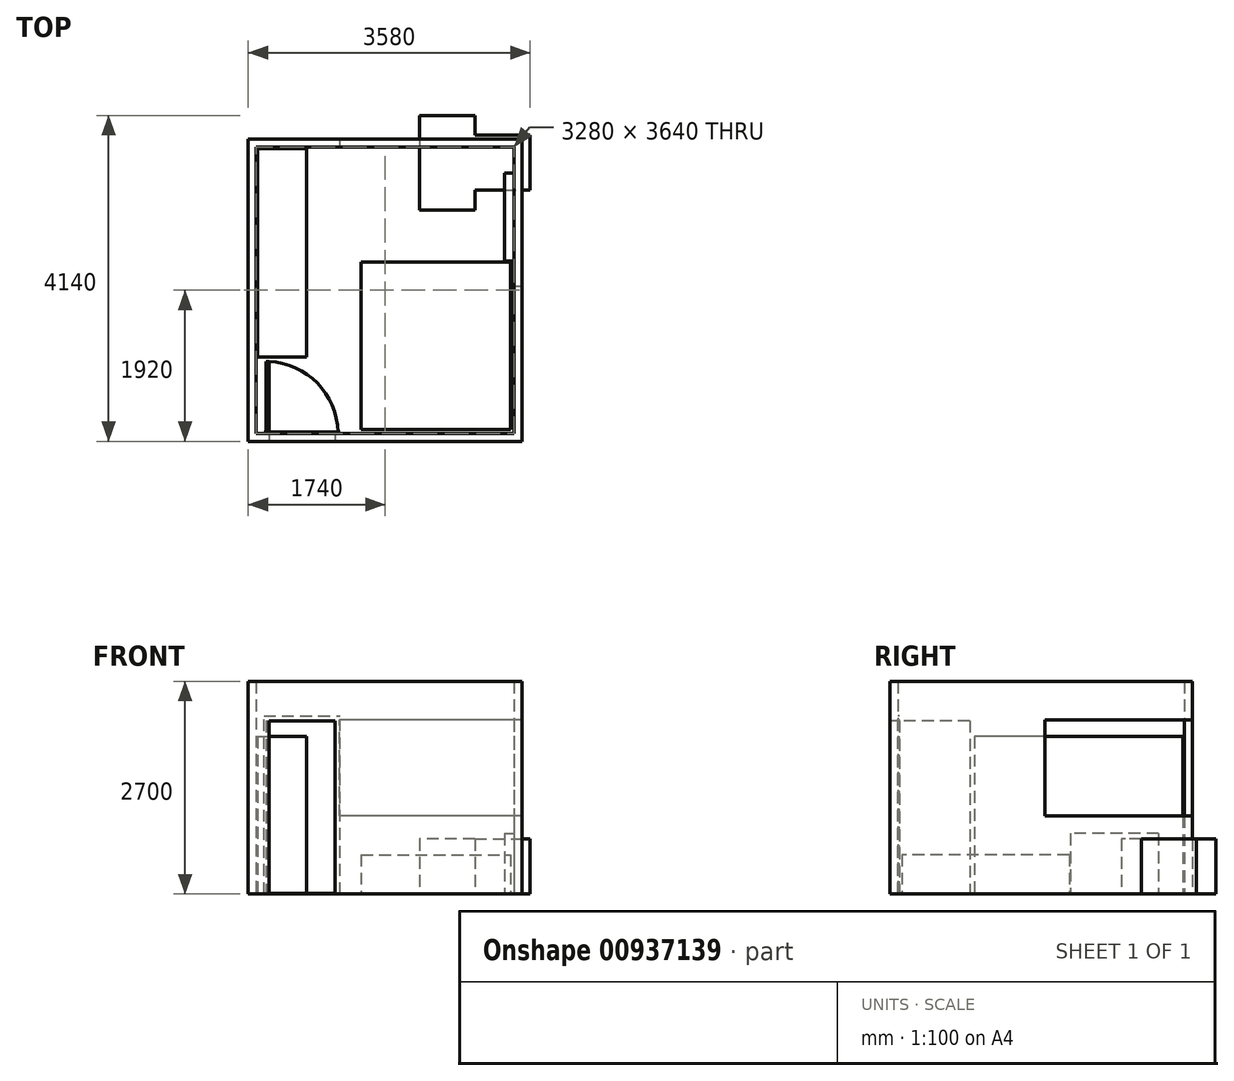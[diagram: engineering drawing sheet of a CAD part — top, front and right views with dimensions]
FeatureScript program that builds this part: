
annotation { "Feature Type Name" : "Feature", "Feature Type Description" : "" }
export const myFeature = defineFeature(function(context is Context, id is Id, definition is map)
    precondition{}
    {
        {
            var Q0;
            Q0=qCreatedBy(makeId("Top.planeOp"),FACE);
            var sketch = newSketch(context, id + "F0", { "sketchPlane" : qUnion([Q0])});
            skLineSegment(sketch, "E0.bottom", {"start": v(-3280, 3640) * mm, "end": v(0, 3640) * mm});
            skLineSegment(sketch, "E0.top", {"start": v(-3280, 0) * mm, "end": v(0, 0) * mm});
            skLineSegment(sketch, "E0.left", {"start": v(-3280, 3640) * mm, "end": v(-3280, 0) * mm});
            skLineSegment(sketch, "E0.right", {"start": v(0, 3640) * mm, "end": v(0, 0) * mm});
            skLineSegment(sketch, "E1.0", {"start": v(-3380, 3740) * mm, "end": v(100, 3740) * mm});
            skLineSegment(sketch, "E1.1", {"start": v(-3380, 3740) * mm, "end": v(-3380, -100) * mm});
            skLineSegment(sketch, "E1.2", {"start": v(-3380, -100) * mm, "end": v(100, -100) * mm});
            skLineSegment(sketch, "E1.3", {"start": v(100, 3740) * mm, "end": v(100, -100) * mm});
            skSolve(sketch);
        }
        {
            var Q0;
            Q0=makeQuery(id+"F0.imprint","IMPRINT",FACE,{"disambiguationData":[TD([[makeQuery(id+"F0.imprint","IMPRINT",EDGE,{"derivedFrom":sQuery(id+"F0.wireOp",EDGE,"E0.bottom")}),1.0]])]});
            extrude(context, id + "F1", {"entities" : qUnion([Q0]), "depth" : 2700 * mm, "offsetDistance" : 25 * mm});
        }
        {
            var Q0;
            Q0=makeQuery(id+"F1.opExtrude","SWEPT_FACE",FACE,{"disambiguationData":[OSD([sQuery(id+"F0.wireOp",EDGE,"E0.top")])]});
            var sketch = newSketch(context, id + "F2", { "sketchPlane" : qUnion([Q0])});
            skLineSegment(sketch, "E2.bottom", {"start": v(3115, 0) * mm, "end": v(2275, 0) * mm});
            skLineSegment(sketch, "E2.top", {"start": v(3115, 2200) * mm, "end": v(2275, 2200) * mm});
            skLineSegment(sketch, "E2.left", {"start": v(3115, 0) * mm, "end": v(3115, 2200) * mm});
            skLineSegment(sketch, "E2.right", {"start": v(2275, 0) * mm, "end": v(2275, 2200) * mm});
            skLineSegment(sketch, "E3.bottom", {"start": v(3180, 0) * mm, "end": v(2210, 0) * mm});
            skLineSegment(sketch, "E3.top", {"start": v(3180, 2265) * mm, "end": v(2210, 2265) * mm});
            skLineSegment(sketch, "E3.left", {"start": v(3180, 0) * mm, "end": v(3180, 2265) * mm});
            skLineSegment(sketch, "E3.right", {"start": v(2210, 0) * mm, "end": v(2210, 2265) * mm});
            skSolve(sketch);
        }
        {
            var Q0;
            Q0=makeQuery(id+"F2.imprint","IMPRINT",FACE,{"disambiguationData":[TD([[makeQuery(id+"F2.imprint","IMPRINT",EDGE,{"derivedFrom":sQuery(id+"F2.wireOp",EDGE,"E2.top")}),-1.0]])]});
            extrude(context, id + "F3", {"entities" : qUnion([Q0]), "operationType" : NewBodyOperationType.ADD, "depth" : 20 * mm, "offsetDistance" : 25 * mm});
        }
        {
            var Q0;
            {var subQ1=sQuery(id+"F0.wireOp",EDGE,"E0.top");Q0=makeQuery(id+"F3.boolean.opBoolean","SPLIT",FACE,{"disambiguationData":[TD([makeQuery(id+"F3.opExtrude","SWEPT_FACE",FACE,{"disambiguationData":[OSD([sQuery(id+"F2.wireOp",EDGE,"E2.top")])]})])],"derivedFrom":makeQuery(id+"F1.opExtrude","SWEPT_FACE",FACE,{"disambiguationData":[OSD([subQ1])]})});}
            extrude(context, id + "F4", {"entities" : qUnion([Q0]), "operationType" : NewBodyOperationType.REMOVE, "endBound" : BoundingType.UP_TO_NEXT, "oppositeDirection" : true, "depth" : 25 * mm, "offsetDistance" : 25 * mm});
        }
        {
            var Q0;
            Q0=makeQuery(id+"F1.opExtrude","SWEPT_FACE",FACE,{"disambiguationData":[OSD([sQuery(id+"F0.wireOp",EDGE,"E0.right")])]});
            var sketch = newSketch(context, id + "F5", { "sketchPlane" : qUnion([Q0])});
            skLineSegment(sketch, "E4.bottom", {"start": v(-3640, 2210) * mm, "end": v(-1870, 2210) * mm});
            skLineSegment(sketch, "E4.top", {"start": v(-3640, 990) * mm, "end": v(-1870, 990) * mm});
            skLineSegment(sketch, "E4.left", {"start": v(-3640, 2210) * mm, "end": v(-3640, 990) * mm});
            skLineSegment(sketch, "E4.right", {"start": v(-1870, 2210) * mm, "end": v(-1870, 990) * mm});
            skSolve(sketch);
        }
        {
            var Q0;
            Q0 = qSketchRegion(id + "F5", true);
            extrude(context, id + "F6", {"entities" : qUnion([Q0]), "operationType" : NewBodyOperationType.REMOVE, "endBound" : BoundingType.UP_TO_NEXT, "oppositeDirection" : true, "depth" : 25 * mm, "offsetDistance" : 25 * mm});
        }
        {
            var Q0;
            Q0=makeQuery(id+"F6.boolean.opBoolean","MERGE",FACE,{"derivedFrom":[makeQuery(id+"F1.opExtrude","SWEPT_FACE",FACE,{"disambiguationData":[OSD([sQuery(id+"F0.wireOp",EDGE,"E0.bottom")])]})],"fromTools":[makeQuery(id+"F6.opExtrude","SWEPT_FACE",FACE,{"disambiguationData":[OSD([sQuery(id+"F5.wireOp",EDGE,"E4.left")])]})]});
            var sketch = newSketch(context, id + "F7", { "sketchPlane" : qUnion([Q0])});
            skLineSegment(sketch, "E5.bottom", {"start": v(100, 990) * mm, "end": v(-2220, 990) * mm});
            skLineSegment(sketch, "E5.top", {"start": v(100, 2210) * mm, "end": v(-2220, 2210) * mm});
            skLineSegment(sketch, "E5.left", {"start": v(100, 990) * mm, "end": v(100, 2210) * mm});
            skLineSegment(sketch, "E5.right", {"start": v(-2220, 990) * mm, "end": v(-2220, 2210) * mm});
            skSolve(sketch);
        }
        {
            var Q0;
            Q0 = qSketchRegion(id + "F7", true);
            extrude(context, id + "F8", {"entities" : qUnion([Q0]), "operationType" : NewBodyOperationType.REMOVE, "endBound" : BoundingType.UP_TO_NEXT, "oppositeDirection" : true, "depth" : 25 * mm, "offsetDistance" : 25 * mm});
        }
        {
            var Q0;
            Q0=makeQuery(id+"F1.opExtrude","SWEPT_FACE",FACE,{"disambiguationData":[OSD([sQuery(id+"F0.wireOp",EDGE,"E0.right")])]});
            var sketch = newSketch(context, id + "F9", { "sketchPlane" : qUnion([Q0])});
            skLineSegment(sketch, "E6.bottom", {"start": v(-3310, 770) * mm, "end": v(-2190, 770) * mm});
            skLineSegment(sketch, "E6.top", {"start": v(-3310, 0) * mm, "end": v(-2190, 0) * mm});
            skLineSegment(sketch, "E6.left", {"start": v(-3310, 770) * mm, "end": v(-3310, 0) * mm});
            skLineSegment(sketch, "E6.right", {"start": v(-2190, 770) * mm, "end": v(-2190, 0) * mm});
            skSolve(sketch);
        }
        {
            var Q0;
            Q0 = qSketchRegion(id + "F9", true);
            extrude(context, id + "F10", {"entities" : qUnion([Q0]), "operationType" : NewBodyOperationType.ADD, "depth" : 125 * mm, "offsetDistance" : 25 * mm});
        }
        {
            var Q0;
            {var subQ0=sQuery(id+"F2.wireOp",EDGE,"E3.bottom");var subQ1=sQuery(id+"F0.wireOp",EDGE,"E0.top");Q0=makeQuery(id+"F3.boolean.opBoolean","MERGE",FACE,{"derivedFrom":[makeQuery(id+"F1.opExtrude","CAP_FACE",FACE,{"disambiguationData":[OSD([sQuery(id+"F0.wireOp",EDGE,"E0.bottom"),subQ1,sQuery(id+"F0.wireOp",EDGE,"E0.left"),sQuery(id+"F0.wireOp",EDGE,"E0.right"),sQuery(id+"F0.wireOp",EDGE,"E1.0"),sQuery(id+"F0.wireOp",EDGE,"E1.1"),sQuery(id+"F0.wireOp",EDGE,"E1.2"),sQuery(id+"F0.wireOp",EDGE,"E1.3")])],"isStart":true}),makeQuery(id+"F3.opExtrude","SWEPT_FACE",FACE,{"disambiguationData":[OSD([subQ0]),TDD([makeQuery(id+"F2.imprint","IMPRINT",EDGE,{"disambiguationData":[TD([[makeQuery(id+"F2.imprint","INTERSECT",VERTEX,{"derivedFrom":[sQuery(id+"F2.wireOp",EDGE,"E2.left"),subQ0]}),1.0]])],"derivedFrom":subQ0})])]}),makeQuery(id+"F3.opExtrude","SWEPT_FACE",FACE,{"disambiguationData":[OSD([subQ0]),TDD([makeQuery(id+"F2.imprint","IMPRINT",EDGE,{"disambiguationData":[TD([[makeQuery(id+"F2.imprint","INTERSECT",VERTEX,{"derivedFrom":[sQuery(id+"F2.wireOp",EDGE,"E2.right"),subQ0]}),-1.0]])],"derivedFrom":subQ0})])]})]});}
            var sketch = newSketch(context, id + "F11", { "sketchPlane" : qUnion([Q0])});
            skLineSegment(sketch, "E7.bottom", {"start": v(-3115, -20) * mm, "end": v(-3155, -20) * mm});
            skLineSegment(sketch, "E7.top", {"start": v(-3115, -915) * mm, "end": v(-3155, -915) * mm});
            skLineSegment(sketch, "E7.left", {"start": v(-3115, -915) * mm, "end": v(-3115, -20) * mm});
            skLineSegment(sketch, "E7.right", {"start": v(-3155, -915) * mm, "end": v(-3155, -20) * mm});
            skSolve(sketch);
        }
        {
            var Q0;
            Q0 = qSketchRegion(id + "F11", true);
            extrude(context, id + "F12", {"entities" : qUnion([Q0]), "operationType" : NewBodyOperationType.ADD, "oppositeDirection" : true, "depth" : 2200 * mm, "offsetDistance" : 25 * mm});
        }
        {
            var Q0;
            {var subQ0=sQuery(id+"F2.wireOp",EDGE,"E3.bottom");var subQ1=sQuery(id+"F0.wireOp",EDGE,"E0.top");Q0=makeQuery(id+"F10.boolean.opBoolean","MERGE",FACE,{"derivedFrom":[makeQuery(id+"F12.boolean.opBoolean","MERGE",FACE,{"derivedFrom":[makeQuery(id+"F3.boolean.opBoolean","MERGE",FACE,{"derivedFrom":[makeQuery(id+"F1.opExtrude","CAP_FACE",FACE,{"disambiguationData":[OSD([sQuery(id+"F0.wireOp",EDGE,"E0.bottom"),subQ1,sQuery(id+"F0.wireOp",EDGE,"E0.left"),sQuery(id+"F0.wireOp",EDGE,"E0.right"),sQuery(id+"F0.wireOp",EDGE,"E1.0"),sQuery(id+"F0.wireOp",EDGE,"E1.1"),sQuery(id+"F0.wireOp",EDGE,"E1.2"),sQuery(id+"F0.wireOp",EDGE,"E1.3")])],"isStart":true}),makeQuery(id+"F3.opExtrude","SWEPT_FACE",FACE,{"disambiguationData":[OSD([subQ0]),TDD([makeQuery(id+"F2.imprint","IMPRINT",EDGE,{"disambiguationData":[TD([[makeQuery(id+"F2.imprint","INTERSECT",VERTEX,{"derivedFrom":[sQuery(id+"F2.wireOp",EDGE,"E2.left"),subQ0]}),1.0]])],"derivedFrom":subQ0})])]}),makeQuery(id+"F3.opExtrude","SWEPT_FACE",FACE,{"disambiguationData":[OSD([subQ0]),TDD([makeQuery(id+"F2.imprint","IMPRINT",EDGE,{"disambiguationData":[TD([[makeQuery(id+"F2.imprint","INTERSECT",VERTEX,{"derivedFrom":[sQuery(id+"F2.wireOp",EDGE,"E2.right"),subQ0]}),-1.0]])],"derivedFrom":subQ0})])]})]}),makeQuery(id+"F12.opExtrude","CAP_FACE",FACE,{"disambiguationData":[OSD([sQuery(id+"F11.wireOp",EDGE,"E7.bottom"),sQuery(id+"F11.wireOp",EDGE,"E7.top"),sQuery(id+"F11.wireOp",EDGE,"E7.left"),sQuery(id+"F11.wireOp",EDGE,"E7.right")])],"isStart":true})]}),makeQuery(id+"F10.opExtrude","SWEPT_FACE",FACE,{"disambiguationData":[OSD([sQuery(id+"F9.wireOp",EDGE,"E6.top")])]})]});}
            var sketch = newSketch(context, id + "F13", { "sketchPlane" : qUnion([Q0])});
            skArc(sketch, "E8", {"start": v(-3115, -915) * mm, "mid": v(-2500.34, -640.5) * mm, "end": v(-2239.34, -20) * mm});
            skLineSegment(sketch, "E9", {"start": v(-2239.34, -20) * mm, "end": v(-3115, 0) * mm});
            skLineSegment(sketch, "E10", {"start": v(-3115, 0) * mm, "end": v(-3115, -915) * mm});
            skSolve(sketch);
        }
        {
            var Q0;
            Q0 = qSketchRegion(id + "F13", true);
            extrude(context, id + "F14", {"entities" : qUnion([Q0]), "operationType" : NewBodyOperationType.ADD, "oppositeDirection" : true, "depth" : 10 * mm, "offsetDistance" : 25 * mm});
        }
        {
            var Q0;
            Q0=qCreatedBy(makeId("Top.planeOp"),FACE);
            var sketch = newSketch(context, id + "F15", { "sketchPlane" : qUnion([Q0])});
            skLineSegment(sketch, "E11.bottom", {"start": v(-1945, 2175) * mm, "end": v(-50, 2175) * mm});
            skLineSegment(sketch, "E11.top", {"start": v(-1945, 50) * mm, "end": v(-50, 50) * mm});
            skLineSegment(sketch, "E11.left", {"start": v(-1945, 2175) * mm, "end": v(-1945, 50) * mm});
            skLineSegment(sketch, "E11.right", {"start": v(-50, 2175) * mm, "end": v(-50, 50) * mm});
            skSolve(sketch);
        }
        {
            var Q0;
            Q0 = qSketchRegion(id + "F15", true);
            extrude(context, id + "F16", {"entities" : qUnion([Q0]), "depth" : 500 * mm, "offsetDistance" : 25 * mm});
        }
        {
            var Q0;
            Q0=qCreatedBy(makeId("Top.planeOp"),FACE);
            var sketch = newSketch(context, id + "F17", { "sketchPlane" : qUnion([Q0])});
            skLineSegment(sketch, "E12.bottom", {"start": v(-1700, 2840) * mm, "end": v(-500, 2840) * mm});
            skLineSegment(sketch, "E12.top", {"start": v(-1700, 2140) * mm, "end": v(-500, 2140) * mm});
            skLineSegment(sketch, "E12.left", {"start": v(-1700, 2840) * mm, "end": v(-1700, 2140) * mm});
            skLineSegment(sketch, "E12.right", {"start": v(-500, 2840) * mm, "end": v(-500, 2140) * mm});
            skLineSegment(sketch, "E13.bottom", {"start": v(-1450, 2840) * mm, "end": v(-750, 2840) * mm});
            skLineSegment(sketch, "E13.top", {"start": v(-1450, 3540) * mm, "end": v(-750, 3540) * mm});
            skLineSegment(sketch, "E13.left", {"start": v(-1450, 2840) * mm, "end": v(-1450, 3540) * mm});
            skLineSegment(sketch, "E13.right", {"start": v(-750, 2840) * mm, "end": v(-750, 3540) * mm});
            skPoint(sketch, "E14", {"position": v(-1100, 2840) * mm});
            skSolve(sketch);
        }
        {
            var Q0;
            Q0 = qSketchRegion(id + "F17", true);
            extrude(context, id + "F18", {"entities" : qUnion([Q0]), "depth" : 700 * mm, "offsetDistance" : 25 * mm});
        }
        {
            var Q0;
            Q0=qCreatedBy(makeId("Top.planeOp"),FACE);
            var sketch = newSketch(context, id + "F19", { "sketchPlane" : qUnion([Q0])});
            skLineSegment(sketch, "E15.bottom", {"start": v(-3260, 3620) * mm, "end": v(-2640, 3620) * mm});
            skLineSegment(sketch, "E15.top", {"start": v(-3260, 970) * mm, "end": v(-2640, 970) * mm});
            skLineSegment(sketch, "E15.left", {"start": v(-3260, 3620) * mm, "end": v(-3260, 970) * mm});
            skLineSegment(sketch, "E15.right", {"start": v(-2640, 3620) * mm, "end": v(-2640, 970) * mm});
            skSolve(sketch);
        }
        {
            var Q0;
            Q0 = qSketchRegion(id + "F19", true);
            extrude(context, id + "F20", {"entities" : qUnion([Q0]), "depth" : 2000 * mm, "offsetDistance" : 25 * mm});
        }
        {
            var Q0;
            Q0=makeQuery(id+"F18.opExtrude","SWEPT_BODY",BODY,{"disambiguationData":[OSD([sQuery(id+"F17.wireOp",EDGE,"E12.bottom"),sQuery(id+"F17.wireOp",EDGE,"E12.top"),sQuery(id+"F17.wireOp",EDGE,"E12.left"),sQuery(id+"F17.wireOp",EDGE,"E12.right"),sQuery(id+"F17.wireOp",EDGE,"E13.top"),sQuery(id+"F17.wireOp",EDGE,"E13.left"),sQuery(id+"F17.wireOp",EDGE,"E13.right")])]});
            var Q1;
            Q1=makeQuery(id+"F18.opExtrude","SWEPT_EDGE",EDGE,{"disambiguationData":[OSD([sQuery(id+"F17.wireOp",EDGE,"E12.bottom"),sQuery(id+"F17.wireOp",EDGE,"E12.right")])]});
            transform(context, id + "F21", {"entities" : qUnion([Q0]), "transformType" : TransformType.ROTATION, "transformAxis" : qUnion([Q1]), "angle" : 90 * degree, "makeCopy" : false});
        }
    });
